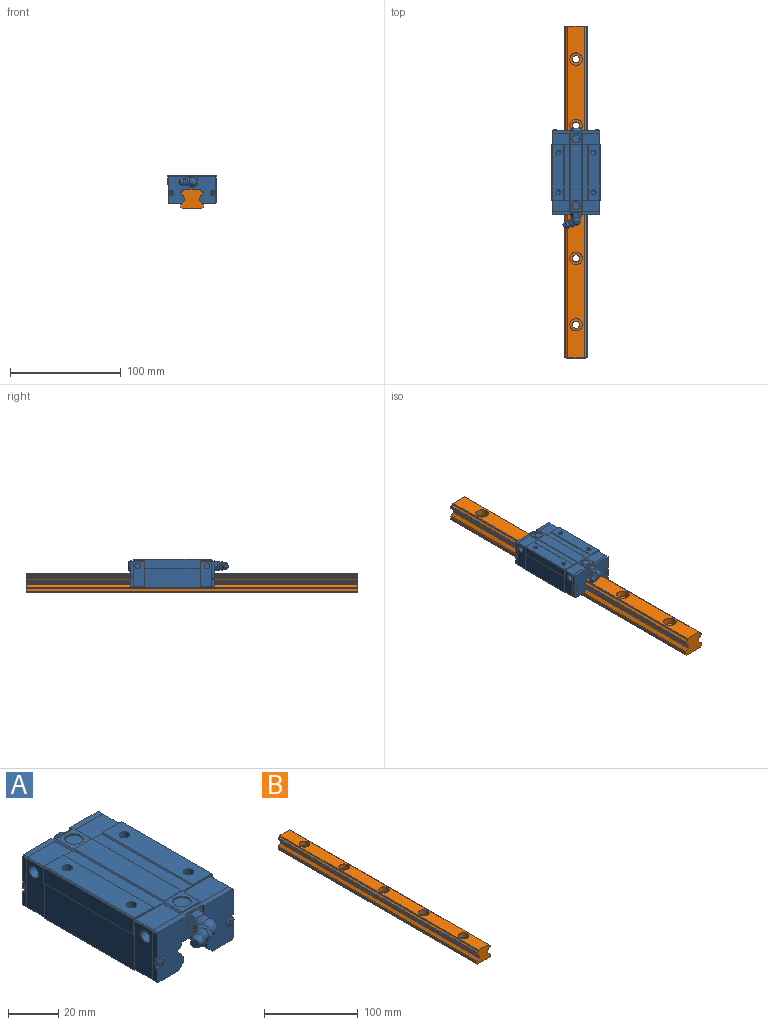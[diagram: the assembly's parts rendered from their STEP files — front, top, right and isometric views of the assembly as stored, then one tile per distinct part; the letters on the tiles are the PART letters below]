
ASSEMBLY  parts=2 mates=1
PART A: 289 faces, bbox 45.6x92x27 mm
  f0: torus R=4.47mm, axis (-0.92,-0.38,0), area 40mm2, adj f19,f20,f22,f141,f142,f143,f144,f145
  f1: cylinder r=2.1mm len=6mm, axis (0,0,-1), area 79.2mm2, adj f2,f264
  f2: cone r=1.05mm half-angle=59deg, axis (0,0,1), area 16.2mm2, adj f1
  f3: cylinder r=2.1mm len=6mm, axis (0,0,-1), area 79.2mm2, adj f4,f264
  f4: cone r=1.05mm half-angle=59deg, axis (0,0,1), area 16.2mm2, adj f3
  f5: cylinder r=2.1mm len=6mm, axis (0,0,-1), area 79.2mm2, adj f6,f263
  f6: cone r=1.05mm half-angle=59deg, axis (0,0,1), area 16.2mm2, adj f5
  f7: cylinder r=2.1mm len=6mm, axis (0,0,-1), area 79.2mm2, adj f8,f263
  f8: cone r=1.05mm half-angle=59deg, axis (0,0,1), area 16.2mm2, adj f7
  f9: cylinder r=3.65mm len=7.3mm, axis (0,0,-1), area 18.2mm2, adj f205,f210
  f10: cylinder r=2.6mm len=6.7mm, axis (-1,0,0), area 109.4mm2, adj f204,f216
  f11: cylinder r=2.6mm len=6.7mm, axis (-1,0,0), area 109.4mm2, adj f203,f212
  f12: cylinder r=2.5mm len=5mm, axis (0,1,0), area 8.6mm2, adj f184,f185,f186,f188
  f13: cylinder r=2.5mm len=5mm, axis (0,1,0), area 8.6mm2, adj f181,f182,f183,f184
  f14: cone r=1.22mm half-angle=5deg, axis (0,1,0), area 19.6mm2, adj f15,f180,f183
  f15: cone r=1.17mm half-angle=73.3deg, axis (0,1,0), area 15.3mm2, adj f14,f168,f169,f170,f171,f172,f173,f174
  f16: cone r=1.22mm half-angle=5deg, axis (0,1,0), area 19.6mm2, adj f17,f166,f188
  f17: cone r=1.17mm half-angle=73.3deg, axis (0,1,0), area 15.3mm2, adj f16,f154,f155,f156,f157,f158,f159,f160
  f18: cone r=2.49mm half-angle=22.5deg, axis (0.92,0.38,0), area 46.5mm2, adj f19,f151
  f19: torus R=0.27mm, axis (-0.92,-0.38,0), area 40mm2, adj f0,f18
  f20: torus R=2.96mm, axis (-0.92,-0.38,0), area 0.2mm2, adj f0,f141,f142
  f21: torus R=2.96mm, axis (-0.92,-0.38,0), area 13.3mm2, adj f141,f142,f143,f144,f145,f146,f152
  f22: torus R=2.96mm, axis (-0.92,-0.38,0), area 0.2mm2, adj f0,f145,f146
  f23: sphere r=3.92mm, area 83.4mm2, adj f24,f152
  f24: cylinder r=3.92mm len=7.85mm, axis (0,1,0), area 87mm2, adj f23,f138,f152
  f25: cone r=4.37mm half-angle=45deg, axis (0,1,0), area 0.9mm2, adj f130,f136,f138
  f26: cone r=4.37mm half-angle=45deg, axis (0,1,0), area 0.9mm2, adj f131,f138,f140
  f27: cone r=4.37mm half-angle=45deg, axis (0,-1,0), area 0.9mm2, adj f130,f136,f192
  f28: cone r=4.37mm half-angle=45deg, axis (0,-1,0), area 0.9mm2, adj f131,f140,f192
  f29: cylinder r=3.65mm len=7.3mm, axis (0,0,-1), area 18.2mm2, adj f101,f114
  f30: cylinder r=2.6mm len=6.7mm, axis (1,0,0), area 109.4mm2, adj f100,f120
  f31: cylinder r=2.6mm len=6.7mm, axis (1,0,0), area 109.4mm2, adj f99,f116
  f32: cylinder r=4.9mm len=9.8mm, axis (0,1,0), area 10.2mm2, adj f33,f88
  f33: torus R=1.93mm, axis (0,-1,0), area 109.6mm2, adj f32,f78,f79,f80,f81,f82,f83
  f34: cylinder r=2.5mm len=5mm, axis (0,-1,0), area 8.6mm2, adj f71,f72,f73,f87
  f35: cylinder r=2.5mm len=5mm, axis (0,-1,0), area 8.6mm2, adj f56,f75,f76,f87
  f36: cone r=1.22mm half-angle=5deg, axis (0,-1,0), area 19.6mm2, adj f37,f57,f71
  f37: cone r=1.17mm half-angle=73.3deg, axis (0,-1,0), area 15.3mm2, adj f36,f59,f60,f61,f62,f63,f64,f65
  f38: cone r=1.22mm half-angle=5deg, axis (0,-1,0), area 19.6mm2, adj f39,f42,f56
  f39: cone r=1.17mm half-angle=73.3deg, axis (0,-1,0), area 15.3mm2, adj f38,f44,f45,f46,f47,f48,f49,f50
  f40: plane 24.4x15.71mm, normal (0,-1,0), area 0.3mm2, adj f74,f91,f92,f93,f96,f110,f112,f116
  f41: plane 24.4x15.71mm, normal (0,-1,0), area 0.3mm2, adj f77,f90,f93,f94,f95,f111,f113,f115
  f42: plane 0.99x0.05mm, normal (0,-1,0), area 0mm2, adj f38,f77
  f43: plane 2.6x2.6mm, normal (0,1,0), area 2.4mm2, adj f44,f45,f46,f47,f48,f49,f50,f51
  f44: plane 1.17x0.58mm, normal (0,0,1), area 0.6mm2, adj f39,f43,f47,f49
  f45: plane 1.17x0.58mm, normal (0,0,-1), area 0.6mm2, adj f39,f43,f46,f48
  f46: plane 1.49x1.47mm, normal (-1,0,0), area 1.3mm2, adj f39,f43,f45,f54
  f47: plane 1.49x1.47mm, normal (-1,0,0), area 1.3mm2, adj f39,f43,f44,f50
  f48: plane 1.49x1.47mm, normal (1,0,0), area 1.3mm2, adj f39,f43,f45,f51
  f49: plane 1.49x1.47mm, normal (1,0,0), area 1.3mm2, adj f39,f43,f44,f52
  f50: plane 1.49x1.47mm, normal (0,0,1), area 1.3mm2, adj f39,f43,f47,f53
  f51: plane 1.49x1.47mm, normal (0,0,-1), area 1.3mm2, adj f39,f43,f48,f55
  f52: plane 1.49x1.47mm, normal (0,0,1), area 1.3mm2, adj f39,f43,f49,f55
  f53: plane 1.17x0.58mm, normal (-1,0,0), area 0.6mm2, adj f39,f43,f50,f54
  f54: plane 1.49x1.47mm, normal (0,0,-1), area 1.3mm2, adj f39,f43,f46,f53
  f55: plane 1.12x0.54mm, normal (1,0,0), area 0.6mm2, adj f39,f43,f51,f52
  f56: plane 5x4.9mm, normal (0,1,0), area 3mm2, adj f35,f38,f75,f76,f77
  f57: plane 0.99x0.05mm, normal (0,-1,0), area 0mm2, adj f36,f74
  f58: plane 2.6x2.6mm, normal (0,1,0), area 2.4mm2, adj f59,f60,f61,f62,f63,f64,f65,f66
  f59: plane 1.17x0.58mm, normal (0,0,1), area 0.6mm2, adj f37,f58,f62,f64
  f60: plane 1.17x0.58mm, normal (0,0,-1), area 0.6mm2, adj f37,f58,f61,f63
  f61: plane 1.49x1.47mm, normal (-1,0,0), area 1.3mm2, adj f37,f58,f60,f69
  f62: plane 1.49x1.47mm, normal (-1,0,0), area 1.3mm2, adj f37,f58,f59,f65
  f63: plane 1.49x1.47mm, normal (1,0,0), area 1.3mm2, adj f37,f58,f60,f66
  f64: plane 1.49x1.47mm, normal (1,0,0), area 1.3mm2, adj f37,f58,f59,f67
  f65: plane 1.49x1.47mm, normal (0,0,1), area 1.3mm2, adj f37,f58,f62,f68
  f66: plane 1.49x1.47mm, normal (0,0,-1), area 1.3mm2, adj f37,f58,f63,f70
  f67: plane 1.49x1.47mm, normal (0,0,1), area 1.3mm2, adj f37,f58,f64,f70
  f68: plane 1.17x0.58mm, normal (-1,0,0), area 0.6mm2, adj f37,f58,f65,f69
  f69: plane 1.49x1.47mm, normal (0,0,-1), area 1.3mm2, adj f37,f58,f61,f68
  f70: plane 1.12x0.54mm, normal (1,0,0), area 0.6mm2, adj f37,f58,f66,f67
  f71: plane 5x4.9mm, normal (0,1,0), area 3mm2, adj f34,f36,f72,f73,f74
  f72: plane 2.4x1.1mm, normal (0,0,-1), area 2.6mm2, adj f34,f71,f74,f87
  f73: plane 2.4x1.1mm, normal (0,0,1), area 2.6mm2, adj f34,f71,f74,f87
  f74: plane 23.4x2.5mm, normal (1,0,0), area 53mm2, adj f40,f57,f71,f72,f73,f87,f92,f96
  f75: plane 2.4x1.1mm, normal (0,0,-1), area 2.6mm2, adj f35,f56,f77,f87
  f76: plane 2.4x1.1mm, normal (0,0,1), area 2.6mm2, adj f35,f56,f77,f87
  f77: plane 23.4x2.5mm, normal (-1,0,0), area 53mm2, adj f41,f42,f56,f75,f76,f87,f94,f95
  f78: plane 2.67x2.48mm, normal (1,0,0), area 5.8mm2, adj f33,f79,f82,f84
  f79: plane 2.5x2mm, normal (0.5,0,0.87), area 5.8mm2, adj f33,f78,f80,f84
  f80: plane 2.5x2mm, normal (-0.5,0,0.87), area 5.8mm2, adj f33,f79,f81,f84
  f81: plane 2.67x2.48mm, normal (-1,0,0), area 5.8mm2, adj f33,f80,f83,f84
  f82: plane 2.5x2mm, normal (0.5,0,-0.87), area 5.8mm2, adj f33,f78,f83,f84
  f83: plane 2.5x2mm, normal (-0.5,0,-0.87), area 5.8mm2, adj f33,f81,f82,f84
  f84: plane 4.62x4mm, normal (0,1,0), area 13.9mm2, adj f78,f79,f80,f81,f82,f83
  f85: plane 5x1.1mm, normal (1,0,0), area 5.5mm2, adj f87,f88,f89,f93
  f86: plane 5x1.1mm, normal (-1,0,0), area 5.5mm2, adj f87,f88,f89,f93
  f87: plane 43x24.4mm, normal (0,1,0), area 707.4mm2, adj f34,f35,f72,f73,f74,f75,f76,f77
  f88: plane 10x10mm, normal (0,1,0), area 13.8mm2, adj f32,f85,f86,f89,f93
  f89: cylinder r=5mm len=10mm, axis (0,-1,0), area 17.3mm2, adj f85,f86,f87,f88
  f90: plane 11.53x2.5mm, normal (0,0,-1), area 28.8mm2, adj f41,f87,f95,f220
  f91: plane 11.53x2.5mm, normal (0,0,-1), area 28.8mm2, adj f40,f87,f96,f246
  f92: plane 2.5x0.5mm, normal (0.71,0,0.71), area 1.8mm2, adj f40,f74,f87,f93
  f93: plane 42x2.5mm, normal (0,0,1), area 94mm2, adj f40,f41,f85,f86,f87,f88,f92,f94
  f94: plane 2.5x0.5mm, normal (-0.71,0,0.71), area 1.8mm2, adj f41,f77,f87,f93
  f95: plane 2.5x0.5mm, normal (-0.71,0,-0.71), area 1.8mm2, adj f41,f77,f87,f90
  f96: plane 2.5x0.5mm, normal (0.71,0,-0.71), area 1.8mm2, adj f40,f74,f87,f91
  f97: plane 6.33x0.8mm, normal (0,-1,0), area 4.7mm2, adj f110,f246,f248,f250
  f98: plane 6.33x0.8mm, normal (0,-1,0), area 4.7mm2, adj f111,f220,f249,f251
  f99: plane 5.2x5.2mm, normal (1,0,0), area 21.2mm2, adj f31
  f100: plane 5.2x5.2mm, normal (-1,0,0), area 21.2mm2, adj f30
  f101: plane 7.3x7.3mm, normal (0,0,1), area 41.9mm2, adj f29
  f102: cylinder r=0.5mm len=75.5mm, axis (0,-1,0), area 31.2mm2, adj f87,f184,f241,f242
  f103: cylinder r=0.5mm len=75.5mm, axis (0,-1,0), area 22.5mm2, adj f87,f184,f240,f241
  f104: cylinder r=0.5mm len=75.5mm, axis (0,-1,0), area 22.3mm2, adj f87,f184,f235,f236
  f105: cylinder r=0.5mm len=75.5mm, axis (0,-1,0), area 31mm2, adj f87,f184,f234,f235
  f106: cylinder r=0.5mm len=75.5mm, axis (0,-1,0), area 31mm2, adj f87,f184,f231,f232
  f107: cylinder r=0.5mm len=75.5mm, axis (0,-1,0), area 22.3mm2, adj f87,f184,f230,f231
  f108: cylinder r=0.5mm len=75.5mm, axis (0,-1,0), area 22.5mm2, adj f87,f184,f225,f226
  f109: cylinder r=0.5mm len=75.5mm, axis (0,-1,0), area 31.2mm2, adj f87,f184,f224,f225
  f110: plane 11.53x10mm, normal (0,0,-1), area 115.3mm2, adj f40,f97,f122,f246,f254
  f111: plane 11.53x10mm, normal (0,0,-1), area 115.3mm2, adj f41,f98,f121,f220,f254
  f112: plane 10x0.8mm, normal (0.71,0,0.71), area 11.2mm2, adj f40,f114,f118,f123,f254
  f113: plane 10x0.8mm, normal (-0.71,0,0.71), area 11.2mm2, adj f41,f114,f115,f123,f254
  f114: plane 10x10mm, normal (0,0,1), area 58.1mm2, adj f29,f112,f113,f123,f254
  f115: plane 15.2x10mm, normal (0,0,1), area 152mm2, adj f41,f113,f119,f254
  f116: plane 23.39x10mm, normal (1,0,0), area 212.7mm2, adj f31,f40,f117,f122,f254
  f117: plane 10x0.5mm, normal (0.71,0,0.71), area 7.1mm2, adj f40,f116,f118,f254
  f118: plane 15.2x10mm, normal (0,0,1), area 152mm2, adj f40,f112,f117,f254
  f119: plane 10x0.5mm, normal (-0.71,0,0.71), area 7.1mm2, adj f41,f115,f120,f254
  f120: plane 23.39x10mm, normal (-1,0,0), area 212.7mm2, adj f30,f41,f119,f121,f254
  f121: plane 10x0.5mm, normal (-0.71,0,-0.71), area 7.1mm2, adj f41,f111,f120,f254
  f122: plane 10x0.5mm, normal (0.71,0,-0.71), area 7.1mm2, adj f40,f110,f116,f254
  f123: plane 11.58x0.79mm, normal (0,1,0), area 8.5mm2, adj f93,f112,f113,f114
  f124: plane 24.4x15.71mm, normal (0,1,0), area 0.3mm2, adj f189,f195,f196,f197,f200,f206,f208,f212
  f125: plane 24.4x15.71mm, normal (0,1,0), area 0.3mm2, adj f187,f194,f197,f198,f199,f207,f209,f211
  f126: cone r=4.37mm half-angle=45deg, axis (0,-1,0), area 0.9mm2, adj f136,f139,f192
  f127: cone r=4.37mm half-angle=45deg, axis (0,-1,0), area 0.9mm2, adj f139,f140,f192
  f128: cone r=4.37mm half-angle=45deg, axis (0,-1,0), area 0.9mm2, adj f131,f137,f192
  f129: cone r=4.37mm half-angle=45deg, axis (0,-1,0), area 0.9mm2, adj f130,f137,f192
  f130: plane 4.15x4.15mm, normal (0.87,0,-0.5), area 17.3mm2, adj f25,f27,f129,f135,f136,f137,f138,f192
  f131: plane 4.15x4.15mm, normal (-0.87,0,-0.5), area 17.3mm2, adj f26,f28,f128,f132,f137,f138,f140,f192
  f132: cone r=4.37mm half-angle=45deg, axis (0,1,0), area 0.9mm2, adj f131,f137,f138
  f133: cone r=4.37mm half-angle=45deg, axis (0,1,0), area 0.9mm2, adj f138,f139,f140
  f134: cone r=4.37mm half-angle=45deg, axis (0,1,0), area 0.9mm2, adj f136,f138,f139
  f135: cone r=4.37mm half-angle=45deg, axis (0,1,0), area 0.9mm2, adj f130,f137,f138
  f136: plane 4.15x4.15mm, normal (0.87,0,0.5), area 17.3mm2, adj f25,f27,f126,f130,f134,f138,f139,f192
  f137: plane 4.77x4.15mm, normal (0,0,-1), area 17.3mm2, adj f128,f129,f130,f131,f132,f135,f138,f192
  f138: plane 8.24x8mm, normal (0,-1,0), area 4mm2, adj f24,f25,f26,f130,f131,f132,f133,f134
  f139: plane 4.77x4.15mm, normal (0,0,1), area 17.3mm2, adj f126,f127,f133,f134,f136,f138,f140,f192
  f140: plane 4.15x4.15mm, normal (-0.87,0,0.5), area 17.3mm2, adj f26,f28,f127,f131,f133,f138,f139,f192
  f141: plane 3.49x2.46mm, normal (0.33,-0.8,0.5), area 7.2mm2, adj f0,f20,f21,f142,f144,f147
  f142: plane 3.49x2.46mm, normal (0.33,-0.8,-0.5), area 7.2mm2, adj f0,f20,f21,f141,f143,f150
  f143: plane 4.28x2.94mm, normal (0,0,-1), area 7.2mm2, adj f0,f21,f142,f145,f149,f150
  f144: plane 4.28x2.94mm, normal (0,0,1), area 7.2mm2, adj f0,f21,f141,f146,f147,f148
  f145: plane 3.49x2.46mm, normal (-0.33,0.8,-0.5), area 7.2mm2, adj f0,f21,f22,f143,f146,f149
  f146: plane 3.49x2.46mm, normal (-0.33,0.8,0.5), area 7.2mm2, adj f0,f21,f22,f144,f145,f148
  f147: torus R=2.96mm, axis (-0.92,-0.38,0), area 0.2mm2, adj f0,f141,f144
  f148: torus R=2.96mm, axis (-0.92,-0.38,0), area 0.2mm2, adj f0,f144,f146
  f149: torus R=2.96mm, axis (-0.92,-0.38,0), area 0.2mm2, adj f0,f143,f145
  f150: torus R=2.96mm, axis (-0.92,-0.38,0), area 0.2mm2, adj f0,f142,f143
  f151: plane 3.84x3.55mm, normal (-0.92,-0.38,0), area 11.6mm2, adj f18
  f152: plane 7.5x7.05mm, normal (0.92,0.38,0), area 13.6mm2, adj f21,f23,f24
  f153: plane 2.6x2.6mm, normal (0,-1,0), area 2.4mm2, adj f154,f155,f156,f157,f158,f159,f160,f161
  f154: plane 1.17x0.58mm, normal (0,0,1), area 0.6mm2, adj f17,f153,f157,f159
  f155: plane 1.17x0.58mm, normal (0,0,-1), area 0.6mm2, adj f17,f153,f156,f158
  f156: plane 1.49x1.47mm, normal (1,0,0), area 1.3mm2, adj f17,f153,f155,f164
  f157: plane 1.49x1.47mm, normal (1,0,0), area 1.3mm2, adj f17,f153,f154,f160
  f158: plane 1.49x1.47mm, normal (-1,0,0), area 1.3mm2, adj f17,f153,f155,f161
  f159: plane 1.49x1.47mm, normal (-1,0,0), area 1.3mm2, adj f17,f153,f154,f162
  f160: plane 1.49x1.47mm, normal (0,0,1), area 1.3mm2, adj f17,f153,f157,f163
  f161: plane 1.49x1.47mm, normal (0,0,-1), area 1.3mm2, adj f17,f153,f158,f165
  f162: plane 1.49x1.47mm, normal (0,0,1), area 1.3mm2, adj f17,f153,f159,f165
  f163: plane 1.17x0.58mm, normal (1,0,0), area 0.6mm2, adj f17,f153,f160,f164
  f164: plane 1.49x1.47mm, normal (0,0,-1), area 1.3mm2, adj f17,f153,f156,f163
  f165: plane 1.12x0.54mm, normal (-1,0,0), area 0.6mm2, adj f17,f153,f161,f162
  f166: plane 0.99x0.05mm, normal (0,1,0), area 0mm2, adj f16,f187
  f167: plane 2.6x2.6mm, normal (0,-1,0), area 2.4mm2, adj f168,f169,f170,f171,f172,f173,f174,f175
  f168: plane 1.17x0.58mm, normal (0,0,1), area 0.6mm2, adj f15,f167,f171,f173
  f169: plane 1.17x0.58mm, normal (0,0,-1), area 0.6mm2, adj f15,f167,f170,f172
  f170: plane 1.49x1.47mm, normal (1,0,0), area 1.3mm2, adj f15,f167,f169,f178
  f171: plane 1.49x1.47mm, normal (1,0,0), area 1.3mm2, adj f15,f167,f168,f174
  f172: plane 1.49x1.47mm, normal (-1,0,0), area 1.3mm2, adj f15,f167,f169,f175
  f173: plane 1.49x1.47mm, normal (-1,0,0), area 1.3mm2, adj f15,f167,f168,f176
  f174: plane 1.49x1.47mm, normal (0,0,1), area 1.3mm2, adj f15,f167,f171,f177
  f175: plane 1.49x1.47mm, normal (0,0,-1), area 1.3mm2, adj f15,f167,f172,f179
  f176: plane 1.49x1.47mm, normal (0,0,1), area 1.3mm2, adj f15,f167,f173,f179
  f177: plane 1.17x0.58mm, normal (1,0,0), area 0.6mm2, adj f15,f167,f174,f178
  f178: plane 1.49x1.47mm, normal (0,0,-1), area 1.3mm2, adj f15,f167,f170,f177
  f179: plane 1.12x0.54mm, normal (-1,0,0), area 0.6mm2, adj f15,f167,f175,f176
  f180: plane 0.99x0.05mm, normal (0,1,0), area 0mm2, adj f14,f189
  f181: plane 2.4x1.1mm, normal (0,0,1), area 2.6mm2, adj f13,f183,f184,f189
  f182: plane 2.4x1.1mm, normal (0,0,-1), area 2.6mm2, adj f13,f183,f184,f189
  f183: plane 5x4.9mm, normal (0,-1,0), area 3mm2, adj f13,f14,f181,f182,f189
  f184: plane 43x24.4mm, normal (0,-1,0), area 707.4mm2, adj f12,f13,f102,f103,f104,f105,f106,f107
  f185: plane 2.4x1.1mm, normal (0,0,-1), area 2.6mm2, adj f12,f184,f187,f188
  f186: plane 2.4x1.1mm, normal (0,0,1), area 2.6mm2, adj f12,f184,f187,f188
  f187: plane 23.4x2.5mm, normal (1,0,0), area 53mm2, adj f125,f166,f184,f185,f186,f188,f198,f199
  f188: plane 5x4.9mm, normal (0,-1,0), area 3mm2, adj f12,f16,f185,f186,f187
  f189: plane 23.4x2.5mm, normal (-1,0,0), area 53mm2, adj f124,f180,f181,f182,f183,f184,f196,f200
  f190: plane 5x1.1mm, normal (-1,0,0), area 5.5mm2, adj f184,f192,f193,f197
  f191: plane 5x1.1mm, normal (1,0,0), area 5.5mm2, adj f184,f192,f193,f197
  f192: plane 10x10mm, normal (0,-1,0), area 36.9mm2, adj f27,f28,f126,f127,f128,f129,f130,f131
  f193: cylinder r=5mm len=10mm, axis (0,1,0), area 17.3mm2, adj f184,f190,f191,f192
  f194: plane 11.53x2.5mm, normal (0,0,-1), area 28.8mm2, adj f125,f184,f199,f246
  f195: plane 11.53x2.5mm, normal (0,0,-1), area 28.8mm2, adj f124,f184,f200,f220
  f196: plane 2.5x0.5mm, normal (-0.71,0,0.71), area 1.8mm2, adj f124,f184,f189,f197
  f197: plane 42x2.5mm, normal (0,0,1), area 94mm2, adj f124,f125,f184,f190,f191,f192,f196,f198
  f198: plane 2.5x0.5mm, normal (0.71,0,0.71), area 1.8mm2, adj f125,f184,f187,f197
  f199: plane 2.5x0.5mm, normal (0.71,0,-0.71), area 1.8mm2, adj f125,f184,f187,f194
  f200: plane 2.5x0.5mm, normal (-0.71,0,-0.71), area 1.8mm2, adj f124,f184,f189,f195
  f201: plane 6.33x0.8mm, normal (0,1,0), area 4.7mm2, adj f206,f220,f249,f251
  f202: plane 6.33x0.8mm, normal (0,1,0), area 4.7mm2, adj f207,f246,f248,f250
  f203: plane 5.2x5.2mm, normal (-1,0,0), area 21.2mm2, adj f11
  f204: plane 5.2x5.2mm, normal (1,0,0), area 21.2mm2, adj f10
  f205: plane 7.3x7.3mm, normal (0,0,1), area 41.9mm2, adj f9
  f206: plane 11.53x10mm, normal (0,0,-1), area 115.3mm2, adj f124,f201,f218,f220,f247
  f207: plane 11.53x10mm, normal (0,0,-1), area 115.3mm2, adj f125,f202,f217,f246,f247
  f208: plane 10x0.8mm, normal (-0.71,0,0.71), area 11.2mm2, adj f124,f210,f214,f219,f247
  f209: plane 10x0.8mm, normal (0.71,0,0.71), area 11.2mm2, adj f125,f210,f211,f219,f247
  f210: plane 10x10mm, normal (0,0,1), area 58.1mm2, adj f9,f208,f209,f219,f247
  f211: plane 15.2x10mm, normal (0,0,1), area 152mm2, adj f125,f209,f215,f247
  f212: plane 23.39x10mm, normal (-1,0,0), area 212.7mm2, adj f11,f124,f213,f218,f247
  f213: plane 10x0.5mm, normal (-0.71,0,0.71), area 7.1mm2, adj f124,f212,f214,f247
  f214: plane 15.2x10mm, normal (0,0,1), area 152mm2, adj f124,f208,f213,f247
  f215: plane 10x0.5mm, normal (0.71,0,0.71), area 7.1mm2, adj f125,f211,f216,f247
  f216: plane 23.39x10mm, normal (1,0,0), area 212.7mm2, adj f10,f125,f215,f217,f247
  f217: plane 10x0.5mm, normal (0.71,0,-0.71), area 7.1mm2, adj f125,f207,f216,f247
  f218: plane 10x0.5mm, normal (-0.71,0,-0.71), area 7.1mm2, adj f124,f206,f212,f247
  f219: plane 11.58x0.79mm, normal (0,-1,0), area 8.5mm2, adj f197,f208,f209,f210
  f220: plane 75.5x2.58mm, normal (0.71,0,-0.71), area 218mm2, adj f41,f87,f90,f98,f111,f124,f184,f195
  f221: cylinder r=1mm len=75.5mm, axis (0,1,0), area 59.3mm2, adj f87,f184,f220,f222
  f222: plane 75.5x1.56mm, normal (1,0,0), area 117.8mm2, adj f87,f184,f221,f223
  f223: cylinder r=1mm len=75.5mm, axis (0,1,0), area 59.3mm2, adj f87,f184,f222,f224
  f224: plane 75.5x0.74mm, normal (0.71,0,0.71), area 78.7mm2, adj f87,f109,f184,f223
  f225: cylinder r=2mm len=75.5mm, axis (0,1,0), area 179.6mm2, adj f87,f108,f109,f184
  f226: plane 75.5x0.16mm, normal (0.71,0,0.71), area 17.4mm2, adj f87,f108,f184,f227
  f227: cylinder r=0.5mm len=75.5mm, axis (0,1,0), area 29.6mm2, adj f87,f184,f226,f228
  f228: plane 75.5x1.06mm, normal (1,0,0), area 79.8mm2, adj f87,f184,f227,f229
  f229: cylinder r=0.5mm len=75.5mm, axis (0,1,0), area 29.6mm2, adj f87,f184,f228,f230
  f230: plane 75.5x0.18mm, normal (0.71,0,-0.71), area 18.7mm2, adj f87,f107,f184,f229
  f231: cylinder r=2mm len=75.5mm, axis (0,1,0), area 178.2mm2, adj f87,f106,f107,f184
  f232: plane 75.5x0.4mm, normal (0.71,0,-0.71), area 42.9mm2, adj f87,f106,f184,f233
  f233: plane 75.5x14.46mm, normal (0,0,-1), area 1091.8mm2, adj f87,f184,f232,f234
  f234: plane 75.5x0.4mm, normal (-0.71,0,-0.71), area 42.9mm2, adj f87,f105,f184,f233
  f235: cylinder r=2mm len=75.5mm, axis (0,1,0), area 178.2mm2, adj f87,f104,f105,f184
  f236: plane 75.5x0.18mm, normal (-0.71,0,-0.71), area 18.7mm2, adj f87,f104,f184,f237
  f237: cylinder r=0.5mm len=75.5mm, axis (0,1,0), area 29.6mm2, adj f87,f184,f236,f238
  f238: plane 75.5x1.06mm, normal (-1,0,0), area 79.8mm2, adj f87,f184,f237,f239
  f239: cylinder r=0.5mm len=75.5mm, axis (0,1,0), area 29.6mm2, adj f87,f184,f238,f240
  f240: plane 75.5x0.16mm, normal (-0.71,0,0.71), area 17.4mm2, adj f87,f103,f184,f239
  f241: cylinder r=2mm len=75.5mm, axis (0,1,0), area 179.6mm2, adj f87,f102,f103,f184
  f242: plane 75.5x0.74mm, normal (-0.71,0,0.71), area 78.7mm2, adj f87,f102,f184,f243
  f243: cylinder r=1mm len=75.5mm, axis (0,1,0), area 59.3mm2, adj f87,f184,f242,f244
  f244: plane 75.5x1.56mm, normal (-1,0,0), area 117.8mm2, adj f87,f184,f243,f245
  f245: cylinder r=1mm len=75.5mm, axis (0,1,0), area 59.3mm2, adj f87,f184,f244,f246
  f246: plane 75.5x2.58mm, normal (-0.71,0,-0.71), area 218mm2, adj f40,f87,f91,f97,f110,f125,f184,f194
  f247: plane 44x25.4mm, normal (0,-1,0), area 47.9mm2, adj f206,f207,f208,f209,f210,f211,f212,f213
  f248: plane 50.5x6.33mm, normal (0,0,-1), area 319.6mm2, adj f97,f202,f246,f250
  f249: plane 50.5x6.33mm, normal (0,0,-1), area 319.6mm2, adj f98,f201,f220,f251
  f250: plane 50.5x0.8mm, normal (-1,0,0), area 40.4mm2, adj f97,f202,f247,f248,f253,f254
  f251: plane 50.5x0.8mm, normal (1,0,0), area 40.4mm2, adj f98,f201,f247,f249,f252,f254
  f252: plane 50.5x6.5mm, normal (0,0,-1), area 328.2mm2, adj f247,f251,f254,f271
  f253: plane 50.5x6.5mm, normal (0,0,-1), area 328.2mm2, adj f247,f250,f254,f270
  f254: plane 44x25.4mm, normal (0,1,0), area 47.9mm2, adj f110,f111,f112,f113,f114,f115,f116,f117
  f255: plane 50.5x0.5mm, normal (-0.71,0,0.71), area 35.7mm2, adj f247,f254,f256,f258
  f256: plane 50.5x10mm, normal (0,0,1), area 505mm2, adj f247,f254,f255,f257
  f257: plane 50.5x0.5mm, normal (0.71,0,0.71), area 35.7mm2, adj f247,f254,f256,f261
  f258: plane 50.5x5.13mm, normal (0,0,1), area 258.8mm2, adj f247,f254,f255,f262
  f259: plane 50.5x7.5mm, normal (-1,0,0), area 378.7mm2, adj f247,f254,f265,f267
  f260: plane 50.5x0.5mm, normal (-0.71,0,0.71), area 35.7mm2, adj f247,f254,f261,f263
  f261: plane 50.5x5.13mm, normal (0,0,1), area 258.8mm2, adj f247,f254,f257,f260
  f262: plane 50.5x0.5mm, normal (0.71,0,0.71), area 35.7mm2, adj f247,f254,f258,f264
  f263: plane 50.5x10.38mm, normal (0,0,1), area 496.2mm2, adj f5,f7,f247,f254,f260,f268
  f264: plane 50.5x10.38mm, normal (0,0,1), area 496.2mm2, adj f1,f3,f247,f254,f262,f267
  f265: plane 50.5x0.4mm, normal (0,0,-1), area 20.2mm2, adj f247,f254,f259,f266
  f266: plane 50.5x17.3mm, normal (-1,0,0), area 873.6mm2, adj f247,f254,f265,f271
  f267: plane 50.5x0.5mm, normal (-0.71,0,0.71), area 35.7mm2, adj f247,f254,f259,f264
  f268: plane 50.5x0.5mm, normal (0.71,0,0.71), area 35.7mm2, adj f247,f254,f263,f269
  f269: plane 50.5x24.4mm, normal (1,0,0), area 1232.2mm2, adj f247,f254,f268,f270
  f270: plane 50.5x0.5mm, normal (0.71,0,-0.71), area 35.7mm2, adj f247,f253,f254,f269
  f271: plane 50.5x0.1mm, normal (-0.71,0,-0.71), area 7.1mm2, adj f247,f252,f254,f266
  f272: cylinder r=3mm len=6mm, axis (0,1,0), area 26.4mm2, adj f274,f275
  f273: cylinder r=3.2mm len=6.4mm, axis (0,1,0), area 28.1mm2, adj f274,f275
  f274: plane 6.4x6.4mm, normal (0,-1,0), area 3.9mm2, adj f272,f273
  f275: plane 6.4x6.4mm, normal (0,1,0), area 3.9mm2, adj f272,f273
  f276: cylinder r=1.25mm len=2.5mm, axis (0,1,0), area 3.9mm2, adj f277,f279
  f277: cone r=0.62mm half-angle=17deg, axis (0,-1,0), area 6.6mm2, adj f276,f280
  f278: cylinder r=1.5mm len=3mm, axis (0,-1,0), area 13.2mm2, adj f279,f280
  f279: plane 3x3mm, normal (0,1,0), area 2.2mm2, adj f276,f278
  f280: plane 3x3mm, normal (0,-1,0), area 4.1mm2, adj f277,f278
  f281: cylinder r=1.5mm len=3mm, axis (0,-1,0), area 13.2mm2, adj f284,f285
  f282: cone r=0.62mm half-angle=17deg, axis (0,-1,0), area 6.6mm2, adj f283,f284
  f283: cylinder r=1.25mm len=2.5mm, axis (0,1,0), area 3.9mm2, adj f282,f285
  f284: plane 3x3mm, normal (0,-1,0), area 4.1mm2, adj f281,f282
  f285: plane 3x3mm, normal (0,1,0), area 2.2mm2, adj f281,f283
  f286: cylinder r=3.2mm len=6.4mm, axis (0,-1,0), area 28.1mm2, adj f287,f288
  f287: plane 6.4x6.4mm, normal (0,1,0), area 32.2mm2, adj f286
  f288: plane 6.4x6.4mm, normal (0,-1,0), area 32.2mm2, adj f286
PART B: 59 faces, bbox 20x300x17.5 mm
  f0: plane 300x1mm, normal (-0.71,0,-0.71), area 424.3mm2, adj f1,f41,f42,f43
  f1: plane 300x18mm, normal (0,0,-1), area 5228.9mm2, adj f0,f2,f42,f43,f44,f47,f50,f53
  f2: plane 300x1mm, normal (0.71,0,-0.71), area 424.3mm2, adj f1,f3,f42,f43
  f3: plane 300x2.66mm, normal (1,0,0), area 797mm2, adj f2,f4,f42,f43
  f4: cylinder r=1mm len=300mm, axis (0,1,0), area 235.6mm2, adj f3,f5,f42,f43
  f5: plane 300x2.81mm, normal (0.71,0,0.71), area 1194mm2, adj f4,f6,f42,f43
  f6: cylinder r=1mm len=300mm, axis (0,1,0), area 235.6mm2, adj f5,f7,f42,f43
  f7: plane 300x1.56mm, normal (1,0,0), area 468mm2, adj f6,f8,f42,f43
  f8: cylinder r=1mm len=300mm, axis (0,1,0), area 235.6mm2, adj f7,f9,f42,f43
  f9: plane 300x0.74mm, normal (0.71,0,-0.71), area 312.8mm2, adj f8,f10,f42,f43
  f10: cylinder r=0.5mm len=300mm, axis (0,1,0), area 124mm2, adj f9,f11,f42,f43
  f11: cylinder r=2mm len=300mm, axis (0,1,0), area 713.8mm2, adj f10,f12,f42,f43
  f12: cylinder r=0.5mm len=300mm, axis (0,1,0), area 89.2mm2, adj f11,f13,f42,f43
  f13: plane 300x0.16mm, normal (0.71,0,-0.71), area 69.1mm2, adj f12,f14,f42,f43
  f14: cylinder r=0.5mm len=300mm, axis (0,1,0), area 117.8mm2, adj f13,f15,f42,f43
  f15: plane 300x1.06mm, normal (1,0,0), area 317.2mm2, adj f14,f16,f42,f43
  f16: cylinder r=0.5mm len=300mm, axis (0,1,0), area 117.8mm2, adj f15,f17,f42,f43
  f17: plane 300x0.18mm, normal (0.71,0,0.71), area 74.3mm2, adj f16,f18,f42,f43
  f18: cylinder r=0.5mm len=300mm, axis (0,1,0), area 88.5mm2, adj f17,f19,f42,f43
  f19: cylinder r=2mm len=300mm, axis (0,1,0), area 708.1mm2, adj f18,f20,f42,f43
  f20: cylinder r=0.5mm len=300mm, axis (0,1,0), area 123mm2, adj f19,f21,f42,f43
  f21: plane 300x0.4mm, normal (0.71,0,0.71), area 170.5mm2, adj f20,f22,f42,f43
  f22: plane 300x14.46mm, normal (0,0,1), area 3841.4mm2, adj f21,f23,f42,f43,f46,f49,f52,f55
  f23: plane 300x0.4mm, normal (-0.71,0,0.71), area 170.5mm2, adj f22,f24,f42,f43
  f24: cylinder r=0.5mm len=300mm, axis (0,1,0), area 123mm2, adj f23,f25,f42,f43
  f25: cylinder r=2mm len=300mm, axis (0,1,0), area 708.1mm2, adj f24,f26,f42,f43
  f26: cylinder r=0.5mm len=300mm, axis (0,1,0), area 88.5mm2, adj f25,f27,f42,f43
  f27: plane 300x0.18mm, normal (-0.71,0,0.71), area 74.3mm2, adj f26,f28,f42,f43
  f28: cylinder r=0.5mm len=300mm, axis (0,1,0), area 117.8mm2, adj f27,f29,f42,f43
  f29: plane 300x1.06mm, normal (-1,0,0), area 317.2mm2, adj f28,f30,f42,f43
  f30: cylinder r=0.5mm len=300mm, axis (0,1,0), area 117.8mm2, adj f29,f31,f42,f43
  f31: plane 300x0.16mm, normal (-0.71,0,-0.71), area 69.1mm2, adj f30,f32,f42,f43
  f32: cylinder r=0.5mm len=300mm, axis (0,1,0), area 89.2mm2, adj f31,f33,f42,f43
  f33: cylinder r=2mm len=300mm, axis (0,1,0), area 713.8mm2, adj f32,f34,f42,f43
  f34: cylinder r=0.5mm len=300mm, axis (0,1,0), area 124mm2, adj f33,f35,f42,f43
  f35: plane 300x0.74mm, normal (-0.71,0,-0.71), area 312.8mm2, adj f34,f36,f42,f43
  f36: cylinder r=1mm len=300mm, axis (0,1,0), area 235.6mm2, adj f35,f37,f42,f43
  f37: plane 300x1.56mm, normal (-1,0,0), area 468mm2, adj f36,f38,f42,f43
  f38: cylinder r=1mm len=300mm, axis (0,1,0), area 235.6mm2, adj f37,f39,f42,f43
  f39: plane 300x2.81mm, normal (-0.71,0,0.71), area 1194mm2, adj f38,f40,f42,f43
  f40: cylinder r=1mm len=300mm, axis (0,1,0), area 235.6mm2, adj f39,f41,f42,f43
  f41: plane 300x2.66mm, normal (-1,0,0), area 797mm2, adj f0,f40,f42,f43
  f42: plane 20x17.5mm, normal (0,-1,0), area 299.1mm2, adj f0,f1,f2,f3,f4,f5,f6,f7
  f43: plane 20x17.5mm, normal (0,1,0), area 299.1mm2, adj f0,f1,f2,f3,f4,f5,f6,f7
  f44: cylinder r=3.3mm len=11.5mm, axis (0,0,1), area 238.4mm2, adj f1,f45
  f45: plane 11.25x11.25mm, normal (0,0,1), area 65.2mm2, adj f44,f46
  f46: cylinder r=5.62mm len=11.25mm, axis (0,0,1), area 212.1mm2, adj f22,f45
  f47: cylinder r=3.3mm len=11.5mm, axis (0,0,1), area 238.4mm2, adj f1,f48
  f48: plane 11.25x11.25mm, normal (0,0,1), area 65.2mm2, adj f47,f49
  f49: cylinder r=5.62mm len=11.25mm, axis (0,0,1), area 212.1mm2, adj f22,f48
  f50: cylinder r=3.3mm len=11.5mm, axis (0,0,1), area 238.4mm2, adj f1,f51
  f51: plane 11.25x11.25mm, normal (0,0,1), area 65.2mm2, adj f50,f52
  f52: cylinder r=5.62mm len=11.25mm, axis (0,0,1), area 212.1mm2, adj f22,f51
  f53: cylinder r=3.3mm len=11.5mm, axis (0,0,1), area 238.4mm2, adj f1,f54
  f54: plane 11.25x11.25mm, normal (0,0,1), area 65.2mm2, adj f53,f55
  f55: cylinder r=5.62mm len=11.25mm, axis (0,0,1), area 212.1mm2, adj f22,f54
  f56: cylinder r=3.3mm len=11.5mm, axis (0,0,1), area 238.4mm2, adj f1,f57
  f57: plane 11.25x11.25mm, normal (0,0,1), area 65.2mm2, adj f56,f58
  f58: cylinder r=5.62mm len=11.25mm, axis (0,0,1), area 212.1mm2, adj f22,f57
PLACE A t=(18.09,42.67,-75.31)mm
PLACE B t=(18.09,62.68,-57.81)mm
MATE slider A.f184 <-> B.f42  axis (0,-1,0) through (18.09,42.72,-57.81)mm
